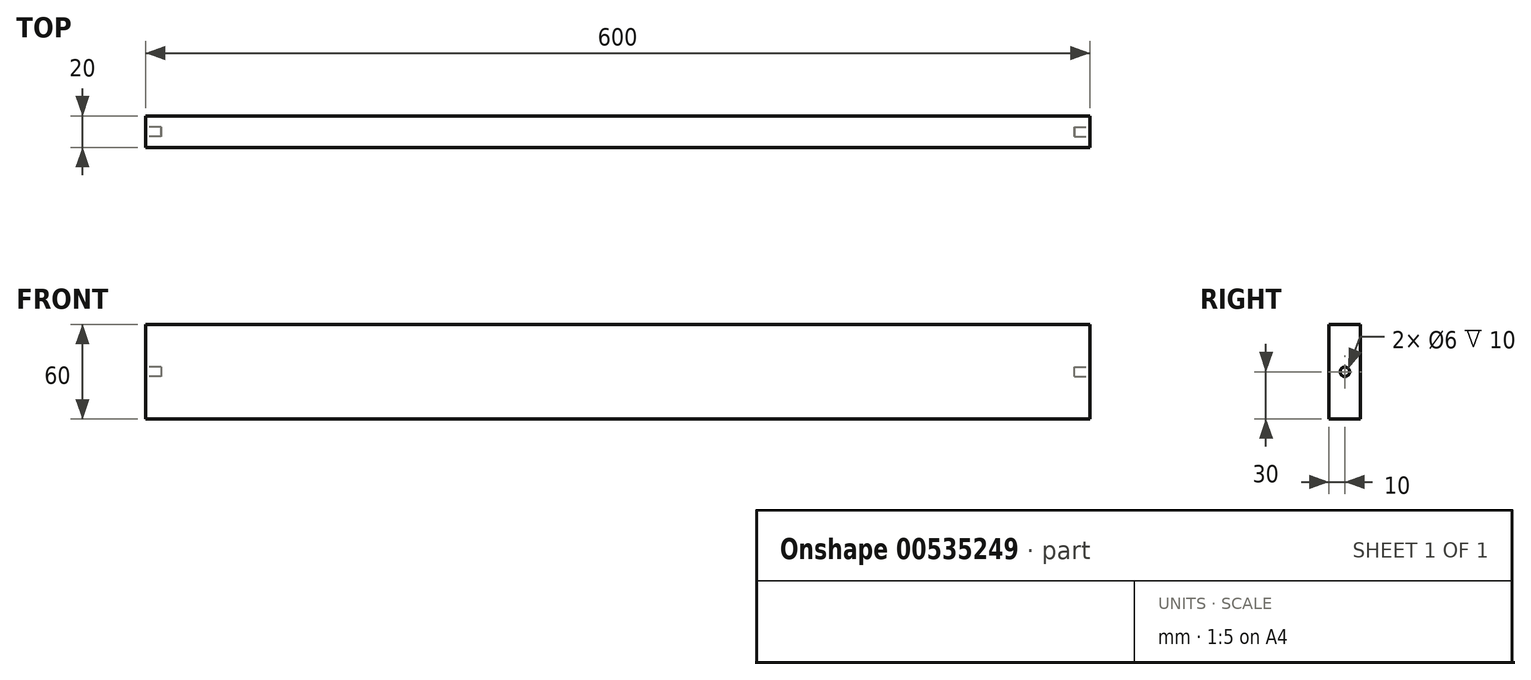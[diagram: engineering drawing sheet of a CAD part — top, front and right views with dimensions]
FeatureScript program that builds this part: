
annotation { "Feature Type Name" : "Feature", "Feature Type Description" : "" }
export const myFeature = defineFeature(function(context is Context, id is Id, definition is map)
    precondition{}
    {
        {
            var Q0;
            Q0=qCreatedBy(makeId("Right.planeOp"),FACE);
            var sketch = newSketch(context, id + "F0", { "sketchPlane" : qUnion([Q0])});
            skLineSegment(sketch, "E0.bottom", {"start": v(0, 0) * mm, "end": v(20, 0) * mm});
            skLineSegment(sketch, "E0.top", {"start": v(0, 60) * mm, "end": v(20, 60) * mm});
            skLineSegment(sketch, "E0.left", {"start": v(0, 0) * mm, "end": v(0, 60) * mm});
            skLineSegment(sketch, "E0.right", {"start": v(20, 0) * mm, "end": v(20, 60) * mm});
            skSolve(sketch);
        }
        {
            var Q0;
            Q0=makeQuery(id+"F0.imprint","IMPRINT",FACE,{"disambiguationData":[TD([[makeQuery(id+"F0.imprint","IMPRINT",EDGE,{"derivedFrom":sQuery(id+"F0.wireOp",EDGE,"E0.bottom")}),1.0]])]});
            extrude(context, id + "F1", {"entities" : qUnion([Q0]), "depth" : 300 * mm, "offsetDistance" : 25 * mm, "hasSecondDirection" : true, "secondDirectionOppositeDirection" : true, "secondDirectionDepth" : 300 * mm});
        }
        {
            var Q0;
            Q0=makeQuery(id+"F1.opExtrude","CAP_FACE",FACE,{"disambiguationData":[OSD([sQuery(id+"F0.wireOp",EDGE,"E0.bottom"),sQuery(id+"F0.wireOp",EDGE,"E0.top"),sQuery(id+"F0.wireOp",EDGE,"E0.left"),sQuery(id+"F0.wireOp",EDGE,"E0.right")])],"isStart":false});
            var sketch = newSketch(context, id + "F2", { "sketchPlane" : qUnion([Q0])});
            skCircle(sketch, "E1", {"center": v(10, 30) * mm, "radius": 3 * mm});
            skPoint(sketch, "E1.centerSnap0", {"position": v(20, 30) * mm});
            skPoint(sketch, "E1.centerSnap1", {"position": v(10, 60) * mm});
            skSolve(sketch);
        }
        {
            var Q0;
            Q0=makeQuery(id+"F2.imprint","IMPRINT",FACE,{"disambiguationData":[TD([[makeQuery(id+"F2.imprint","IMPRINT",EDGE,{"derivedFrom":sQuery(id+"F2.wireOp",EDGE,"E1")}),1.0]])]});
            extrude(context, id + "F3", {"entities" : qUnion([Q0]), "operationType" : NewBodyOperationType.REMOVE, "oppositeDirection" : true, "depth" : 10 * mm, "offsetDistance" : 25 * mm});
        }
        {
            var Q0;
            Q0=makeQuery(id+"F1.opExtrude","CAP_FACE",FACE,{"disambiguationData":[OSD([sQuery(id+"F0.wireOp",EDGE,"E0.bottom"),sQuery(id+"F0.wireOp",EDGE,"E0.top"),sQuery(id+"F0.wireOp",EDGE,"E0.left"),sQuery(id+"F0.wireOp",EDGE,"E0.right")])],"isStart":true});
            var sketch = newSketch(context, id + "F4", { "sketchPlane" : qUnion([Q0])});
            skCircle(sketch, "E2", {"center": v(-10, 30) * mm, "radius": 3 * mm});
            skPoint(sketch, "E2.centerSnap0", {"position": v(-20, 30) * mm});
            skPoint(sketch, "E2.centerSnap1", {"position": v(-10, 60) * mm});
            skSolve(sketch);
        }
        {
            var Q0;
            Q0=makeQuery(id+"F4.imprint","IMPRINT",FACE,{"disambiguationData":[TD([[makeQuery(id+"F4.imprint","IMPRINT",EDGE,{"derivedFrom":sQuery(id+"F4.wireOp",EDGE,"E2")}),1.0]])]});
            extrude(context, id + "F5", {"entities" : qUnion([Q0]), "operationType" : NewBodyOperationType.REMOVE, "oppositeDirection" : true, "depth" : 10 * mm, "offsetDistance" : 25 * mm});
        }
    });
